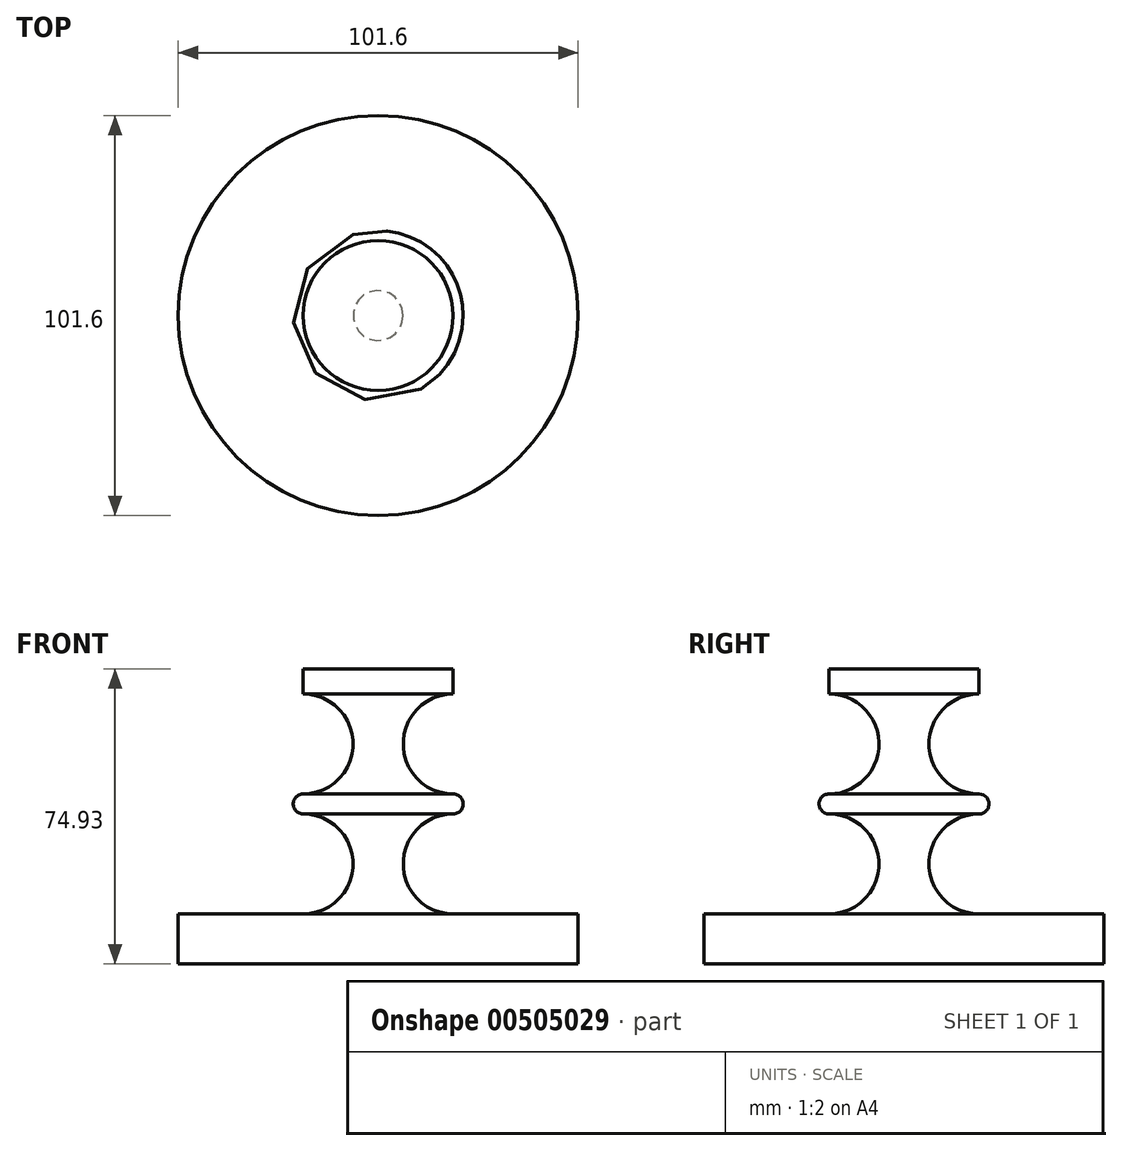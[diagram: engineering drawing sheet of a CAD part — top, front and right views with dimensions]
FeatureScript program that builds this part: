
annotation { "Feature Type Name" : "Feature", "Feature Type Description" : "" }
export const myFeature = defineFeature(function(context is Context, id is Id, definition is map)
    precondition{}
    {
        {
            var Q0;
            Q0=qCreatedBy(makeId("Front.planeOp"),FACE);
            var sketch = newSketch(context, id + "F0", { "sketchPlane" : qUnion([Q0])});
            skLineSegment(sketch, "E0", {"start": v(0, -23.47) * mm, "end": v(50.8, -23.47) * mm});
            skLineSegment(sketch, "E1", {"start": v(50.8, -23.47) * mm, "end": v(50.8, -10.77) * mm});
            skLineSegment(sketch, "E2", {"start": v(50.8, -10.77) * mm, "end": v(19.05, -10.77) * mm});
            skArc(sketch, "E3", {"start": v(19.05, -10.77) * mm, "mid": v(6.35, 1.93) * mm, "end": v(19.05, 14.63) * mm});
            skArc(sketch, "E4", {"start": v(19.05, 14.63) * mm, "mid": v(21.59, 17.17) * mm, "end": v(19.05, 19.71) * mm});
            skArc(sketch, "E5", {"start": v(19.05, 19.71) * mm, "mid": v(6.35, 32.41) * mm, "end": v(19.05, 45.11) * mm});
            skLineSegment(sketch, "E6", {"start": v(19.05, 45.11) * mm, "end": v(19.05, 51.46) * mm});
            skLineSegment(sketch, "E7", {"start": v(19.05, 51.46) * mm, "end": v(0, 51.46) * mm});
            skLineSegment(sketch, "E8", {"start": v(0, 51.46) * mm, "end": v(0, -23.47) * mm});
            skSolve(sketch);
        }
        {
            var Q0;
            Q0=makeQuery(id+"F0.imprint","IMPRINT",FACE,{"disambiguationData":[TD([[makeQuery(id+"F0.imprint","IMPRINT",EDGE,{"derivedFrom":sQuery(id+"F0.wireOp",EDGE,"E0")}),1.0]])]});
            var Q1;
            Q1=sQuery(id+"F0.wireOp",EDGE,"E8");
            revolve(context, id + "F1", {"entities" : qUnion([Q0]), "axis" : qUnion([Q1]), "revolveType" : RevolveType.FULL});
        }
    });
